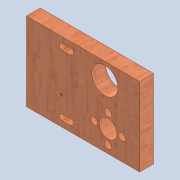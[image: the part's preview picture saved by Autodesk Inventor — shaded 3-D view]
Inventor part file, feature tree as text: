
AUTODESK INVENTOR PART (.ipt)
format: ipt  version: 2020 (Build 240168000, 168)  size: 183,296 bytes
history: native  units: mm
features: extrude x4, sketch x4, other x2, projected_geometry x1, reference x1
ambient origin geometry x8: Origin, YZ Plane, XZ Plane, XY Plane, X Axis, Y Axis, Z Axis, Center Point
bodies: Solid1 (feature_tree)
feature tree (12):
  extrude  "Extrusion1"  Depth=45.0mm
  extrude  "Extrusion3"  Depth=8.0mm
  extrude  "Extrusion4"  Depth=3.5mm
  extrude  "Extrusion5"  TaperAngle=0.0deg  [1 undecoded]
  sketch  "Sketch1"  dims[d0=65.0mm d1=45.0mm]
  sketch  "Sketch3"  dims[d2=8.0mm d3=0.0mm d8=5.0mm]
  projected_geometry  "Projected Loop1"
  sketch  "Sketch4"  dims[d9=3.5mm d10=5.0mm]
  sketch  "Sketch5"  dims[d12=0.0mm d13=0.0mm d14=0.0mm d15=0.0mm d16=5.0mm d17=23.0mm d18=5.0mm d19=8.0mm d20=10.2mm d21=4.1mm d22=4.1mm d23=4.1mm d24=4.1mm d25=22.0mm d26=18.139532mm d27=8.0mm d28=8.0mm d29=8.0mm d30=12.5mm d31=15.0mm d32=23.0mm d33=20.0mm d34=10.0mm d35=0.0mm d36=23.0mm]
  reference  "Reference4"
  other  "0005-10-04 Z axis and extruder.iam"
  other  "0005-10-004 Actionare 2 seringa.ipt:42"
note: 1 required parameter value undecoded (feature->parameter linkage not recoverable at this tier; creation-order binding heuristic only, values carry confidence <= 0.55)
